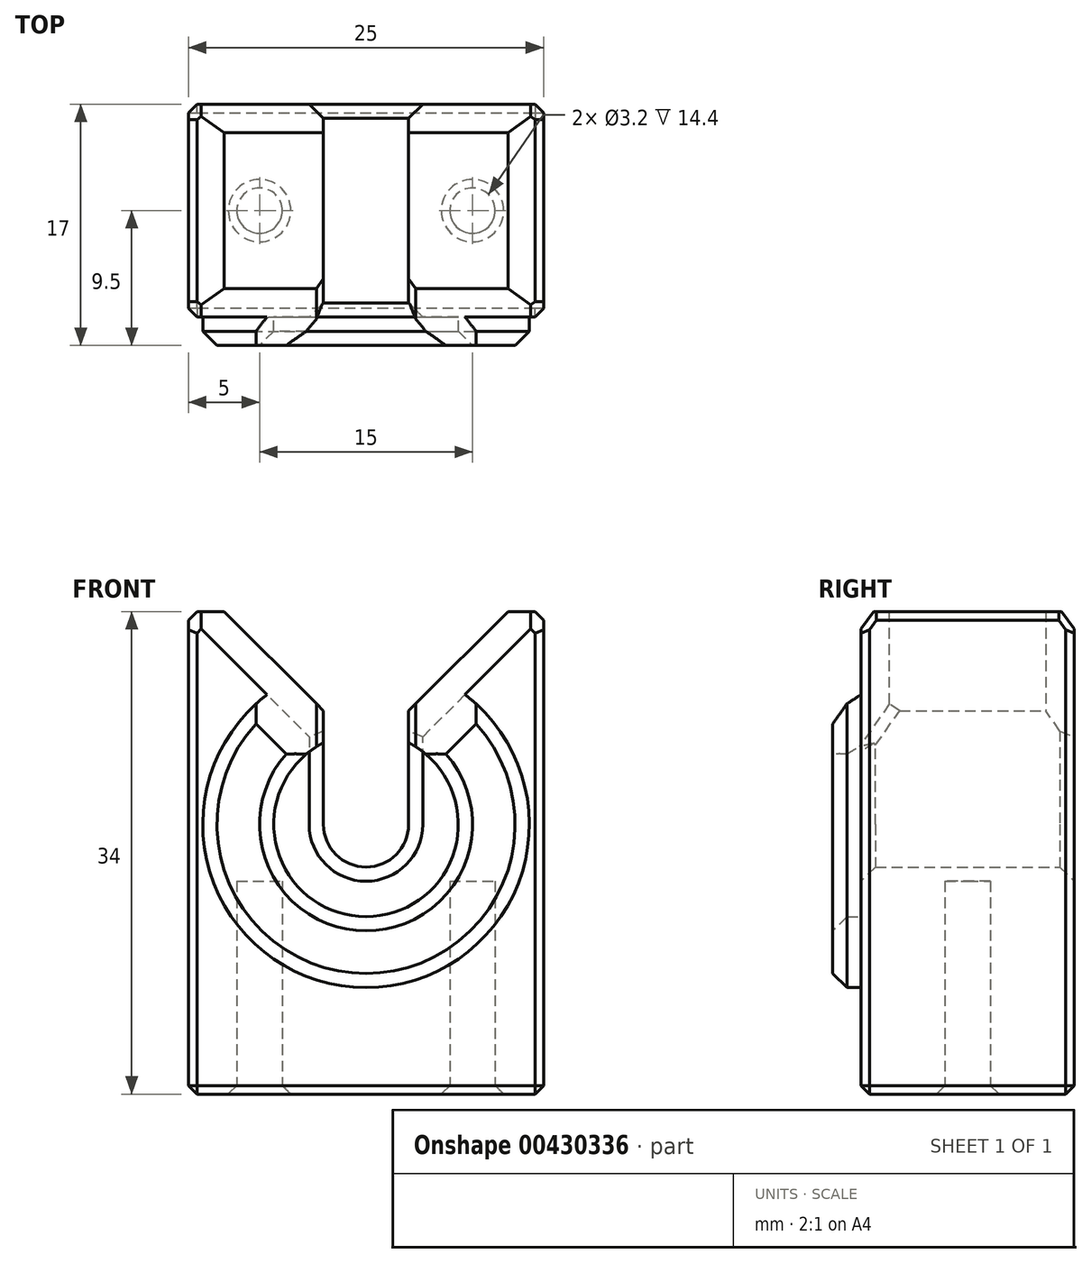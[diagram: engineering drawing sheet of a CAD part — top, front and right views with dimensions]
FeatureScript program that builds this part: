
annotation { "Feature Type Name" : "Feature", "Feature Type Description" : "" }
export const myFeature = defineFeature(function(context is Context, id is Id, definition is map)
    precondition{}
    {
        {
            var Q0;
            Q0=qCreatedBy(makeId("Front.planeOp"),FACE);
            var sketch = newSketch(context, id + "F0", { "sketchPlane" : qUnion([Q0])});
            skLineSegment(sketch, "E0", {"start": v(-12.5, 0) * mm, "end": v(12.5, 0) * mm});
            skLineSegment(sketch, "E1", {"start": v(12.5, 0) * mm, "end": v(12.5, 34) * mm});
            skLineSegment(sketch, "E2", {"start": v(12.5, 34) * mm, "end": v(10, 34) * mm});
            skLineSegment(sketch, "E3", {"start": v(3, 27) * mm, "end": v(3, 19) * mm});
            skLineSegment(sketch, "E4", {"start": v(-3, 19) * mm, "end": v(-3, 27) * mm});
            skLineSegment(sketch, "E5", {"start": v(-10, 34) * mm, "end": v(-12.5, 34) * mm});
            skLineSegment(sketch, "E6", {"start": v(-12.5, 34) * mm, "end": v(-12.5, 0) * mm});
            skLineSegment(sketch, "E7", {"start": v(0, 0) * mm, "end": v(0, 19) * mm, "construction": true});
            skArc(sketch, "E8", {"start": v(3, 19) * mm, "mid": v(0, 16) * mm, "end": v(-3, 19) * mm});
            skLineSegment(sketch, "E9", {"start": v(10, 34) * mm, "end": v(3, 27) * mm});
            skLineSegment(sketch, "E10", {"start": v(-3, 27) * mm, "end": v(-10, 34) * mm});
            skLineSegment(sketch, "E11", {"start": v(-3, 19) * mm, "end": v(3, 19) * mm, "construction": true});
            skSolve(sketch);
        }
        {
            var Q0;
            Q0=qSketchRegion(id+"F0",true);
            extrude(context, id + "F1", {"entities" : qUnion([Q0]), "depth" : 15 * mm, "symmetric" : true});
        }
        {
            var Q0;
            Q0=makeQuery(id+"F1.opExtrude","SWEPT_FACE",FACE,{"disambiguationData":[OSD([sQuery(id+"F0.wireOp",EDGE,"E0")])]});
            var sketch = newSketch(context, id + "F2", { "sketchPlane" : qUnion([Q0])});
            skCircle(sketch, "E12", {"center": v(7.5, 0) * mm, "radius": 1.6 * mm});
            skCircle(sketch, "E13", {"center": v(-7.5, 0) * mm, "radius": 1.6 * mm});
            skSolve(sketch);
        }
        {
            var Q0;
            Q0=qSketchRegion(id+"F2",true);
            extrude(context, id + "F3", {"entities" : qUnion([Q0]), "operationType" : NewBodyOperationType.REMOVE, "oppositeDirection" : true, "depth" : 15 * mm});
        }
        {
            var Q0;
            Q0=makeQuery(id+"F1.opExtrude","CAP_FACE",FACE,{"disambiguationData":[OSD([sQuery(id+"F0.wireOp",EDGE,"E0"),sQuery(id+"F0.wireOp",EDGE,"E1"),sQuery(id+"F0.wireOp",EDGE,"E2"),sQuery(id+"F0.wireOp",EDGE,"E3"),sQuery(id+"F0.wireOp",EDGE,"E4"),sQuery(id+"F0.wireOp",EDGE,"E5"),sQuery(id+"F0.wireOp",EDGE,"E6"),sQuery(id+"F0.wireOp",EDGE,"E8"),sQuery(id+"F0.wireOp",EDGE,"E9"),sQuery(id+"F0.wireOp",EDGE,"E10")])],"isStart":false});
            var sketch = newSketch(context, id + "F4", { "sketchPlane" : qUnion([Q0])});
            skArc(sketch, "E14", {"start": v(-3.38, 24.55) * mm, "mid": v(0, 12.5) * mm, "end": v(3.38, 24.55) * mm});
            skArc(sketch, "E15", {"start": v(-6.97, 28.14) * mm, "mid": v(0, 7.5) * mm, "end": v(6.97, 28.14) * mm});
            skLineSegment(sketch, "E16", {"start": v(-6.97, 28.14) * mm, "end": v(-3.38, 24.55) * mm});
            skLineSegment(sketch, "E17", {"start": v(6.97, 28.14) * mm, "end": v(3.38, 24.55) * mm});
            skSolve(sketch);
        }
        {
            var Q0;
            Q0=qSketchRegion(id+"F4",true);
            extrude(context, id + "F5", {"entities" : qUnion([Q0]), "operationType" : NewBodyOperationType.ADD, "depth" : 2 * mm});
        }
        {
            var Q0;
            Q0=makeQuery(id+"F1.opExtrude","CAP_EDGE",EDGE,{"disambiguationData":[OSD([sQuery(id+"F0.wireOp",EDGE,"E10")])],"isStart":false});
            var Q1;
            Q1=makeQuery(id+"F1.opExtrude","CAP_EDGE",EDGE,{"disambiguationData":[OSD([sQuery(id+"F0.wireOp",EDGE,"E10")])],"isStart":true});
            var Q2;
            Q2=makeQuery(id+"F1.opExtrude","CAP_EDGE",EDGE,{"disambiguationData":[OSD([sQuery(id+"F0.wireOp",EDGE,"E9")])],"isStart":true});
            var Q3;
            Q3=makeQuery(id+"F1.opExtrude","CAP_EDGE",EDGE,{"disambiguationData":[OSD([sQuery(id+"F0.wireOp",EDGE,"E9")])],"isStart":false});
            var Q4;
            Q4=makeQuery(id+"F5.opExtrude","CAP_EDGE",EDGE,{"disambiguationData":[OSD([sQuery(id+"F4.wireOp",EDGE,"E17")])],"isStart":false});
            var Q5;
            Q5=makeQuery(id+"F5.opExtrude","CAP_EDGE",EDGE,{"disambiguationData":[OSD([sQuery(id+"F4.wireOp",EDGE,"E16")])],"isStart":false});
            chamfer(context, id + "F6", {"entities" : qUnion([Q0, Q1, Q2, Q3, Q4, Q5]), "width" : 2 * mm, "tangentPropagation" : true});
        }
        {
            var Q0;
            Q0=makeQuery(id+"F5.opExtrude","CAP_EDGE",EDGE,{"disambiguationData":[OSD([sQuery(id+"F4.wireOp",EDGE,"E15")])],"isStart":false});
            var Q1;
            Q1=makeQuery(id+"F5.opExtrude","CAP_EDGE",EDGE,{"disambiguationData":[OSD([sQuery(id+"F4.wireOp",EDGE,"E14")])],"isStart":false});
            var Q2;
            Q2=makeQuery(id+"F1.opExtrude","CAP_EDGE",EDGE,{"disambiguationData":[OSD([sQuery(id+"F0.wireOp",EDGE,"E8")])],"isStart":false});
            var Q3;
            Q3=makeQuery(id+"F1.opExtrude","CAP_EDGE",EDGE,{"disambiguationData":[OSD([sQuery(id+"F0.wireOp",EDGE,"E3")])],"isStart":true});
            var Q4;
            Q4=makeQuery(id+"F1.opExtrude","CAP_EDGE",EDGE,{"disambiguationData":[OSD([sQuery(id+"F0.wireOp",EDGE,"E4")])],"isStart":true});
            var Q5;
            Q5=makeQuery(id+"F1.opExtrude","CAP_EDGE",EDGE,{"disambiguationData":[OSD([sQuery(id+"F0.wireOp",EDGE,"E8")])],"isStart":true});
            var Q6;
            Q6=makeQuery(id+"F1.opExtrude","CAP_EDGE",EDGE,{"disambiguationData":[OSD([sQuery(id+"F0.wireOp",EDGE,"E4")])],"isStart":false});
            var Q7;
            Q7=makeQuery(id+"F6.opChamfer","BLEND_EDGE",EDGE,{"blendedFrom":[makeQuery(id+"F1.opExtrude","CAP_EDGE",EDGE,{"disambiguationData":[OSD([sQuery(id+"F0.wireOp",EDGE,"E10")])],"isStart":false}),makeQuery(id+"F1.opExtrude","SWEPT_FACE",FACE,{"disambiguationData":[OSD([sQuery(id+"F0.wireOp",EDGE,"E4")])]})],"blendedInto":[makeQuery(id+"F1.opExtrude","SWEPT_FACE",FACE,{"disambiguationData":[OSD([sQuery(id+"F0.wireOp",EDGE,"E4")])]})]});
            var Q8;
            Q8=makeQuery(id+"F6.opChamfer","BLEND_EDGE",EDGE,{"blendedFrom":[makeQuery(id+"F1.opExtrude","CAP_EDGE",EDGE,{"disambiguationData":[OSD([sQuery(id+"F0.wireOp",EDGE,"E9")])],"isStart":false}),makeQuery(id+"F1.opExtrude","SWEPT_FACE",FACE,{"disambiguationData":[OSD([sQuery(id+"F0.wireOp",EDGE,"E3")])]})],"blendedInto":[makeQuery(id+"F1.opExtrude","SWEPT_FACE",FACE,{"disambiguationData":[OSD([sQuery(id+"F0.wireOp",EDGE,"E3")])]})]});
            var Q9;
            Q9=makeQuery(id+"F1.opExtrude","CAP_EDGE",EDGE,{"disambiguationData":[OSD([sQuery(id+"F0.wireOp",EDGE,"E3")])],"isStart":false});
            chamfer(context, id + "F7", {"entities" : qUnion([Q0, Q1, Q2, Q3, Q4, Q5, Q6, Q7, Q8, Q9]), "width" : 1 * mm, "tangentPropagation" : true});
        }
        {
            var Q0;
            Q0=makeQuery(id+"F1.opExtrude","SWEPT_FACE",FACE,{"disambiguationData":[OSD([sQuery(id+"F0.wireOp",EDGE,"E6")])]});
            var Q1;
            Q1=makeQuery(id+"F1.opExtrude","SWEPT_FACE",FACE,{"disambiguationData":[OSD([sQuery(id+"F0.wireOp",EDGE,"E1")])]});
            var Q2;
            Q2=makeQuery(id+"F1.opExtrude","SWEPT_FACE",FACE,{"disambiguationData":[OSD([sQuery(id+"F0.wireOp",EDGE,"E0")])]});
            chamfer(context, id + "F8", {"entities" : qUnion([Q0, Q1, Q2]), "width" : 0.6 * mm, "tangentPropagation" : true});
        }
    });
